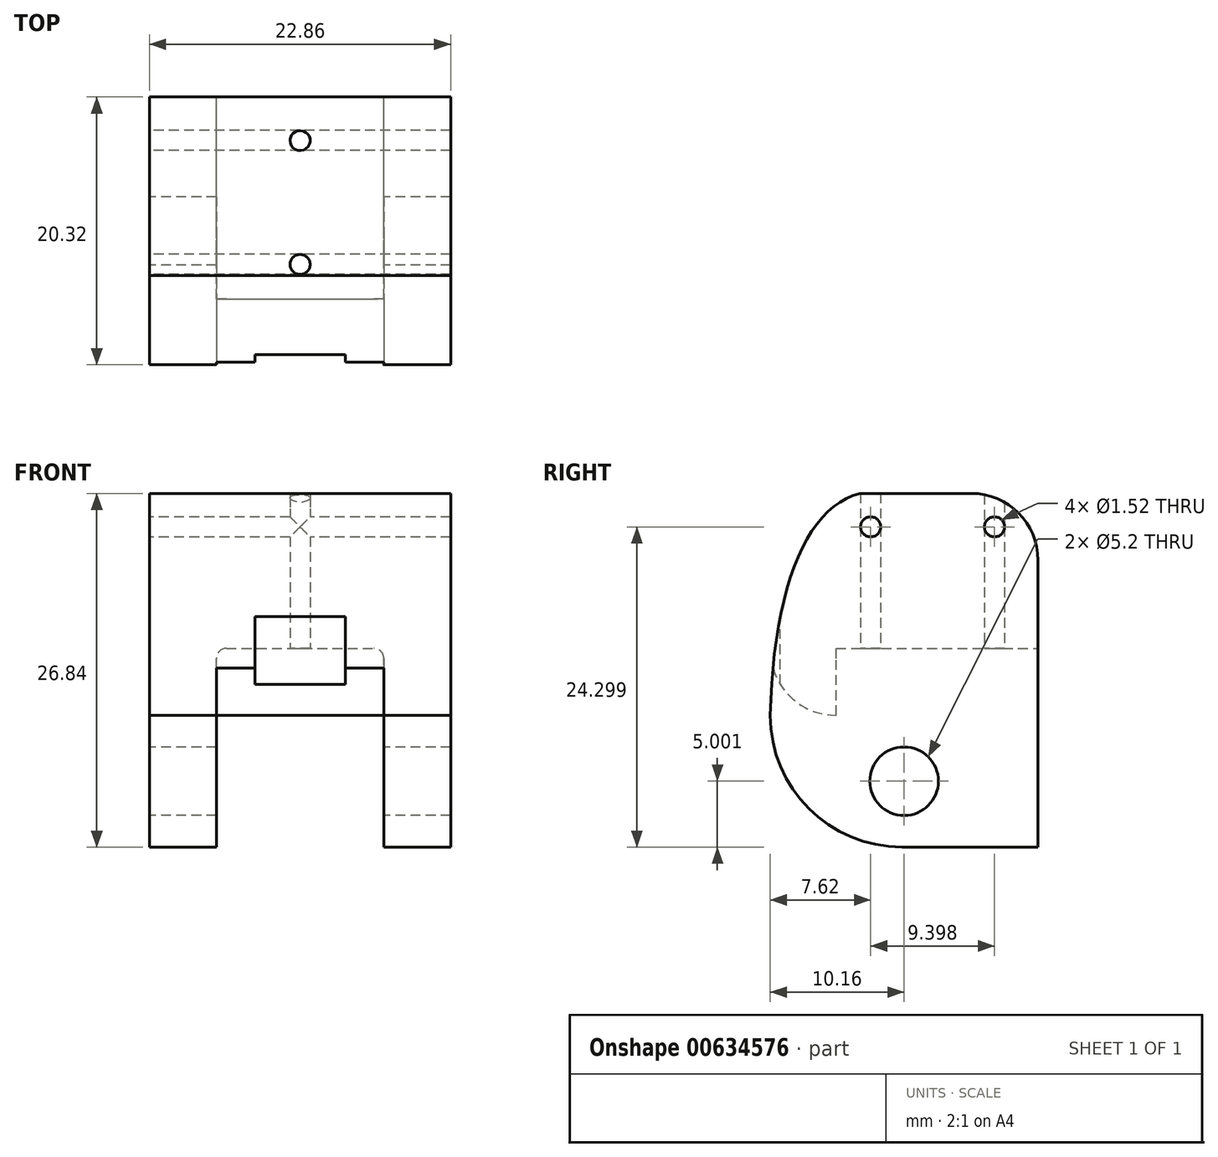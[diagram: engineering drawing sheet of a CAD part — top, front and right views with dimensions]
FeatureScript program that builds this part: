
annotation { "Feature Type Name" : "Feature", "Feature Type Description" : "" }
export const myFeature = defineFeature(function(context is Context, id is Id, definition is map)
    precondition{}
    {
        {
            var Q0;
            Q0=qCreatedBy(makeId("Front.planeOp"),FACE);
            var sketch = newSketch(context, id + "F0", { "sketchPlane" : qUnion([Q0])});
            skLineSegment(sketch, "E0.top", {"start": v(11.43, -13.42) * mm, "end": v(6.35, -13.42) * mm});
            skLineSegment(sketch, "E0.left", {"start": v(11.43, 13.42) * mm, "end": v(11.43, -13.42) * mm});
            skLineSegment(sketch, "E0.right", {"start": v(-11.43, 13.42) * mm, "end": v(-11.43, -13.42) * mm});
            skPoint(sketch, "E0.middle", {"position": v(0, 0) * mm});
            skLineSegment(sketch, "E1.left", {"start": v(6.35, -13.42) * mm, "end": v(6.35, -3.42) * mm});
            skLineSegment(sketch, "E2.trimOffspring", {"start": v(-6.35, -13.42) * mm, "end": v(-11.43, -13.42) * mm});
            skLineSegment(sketch, "E3", {"start": v(-11.43, 13.42) * mm, "end": v(11.43, 13.42) * mm});
            skLineSegment(sketch, "E4", {"start": v(-6.35, -13.42) * mm, "end": v(-6.35, -3.42) * mm});
            skLineSegment(sketch, "E5", {"start": v(-6.35, -3.42) * mm, "end": v(6.35, -3.42) * mm});
            skSolve(sketch);
        }
        {
            var Q0;
            Q0=makeQuery(id+"F0.imprint","IMPRINT",FACE,{"disambiguationData":[TD([[makeQuery(id+"F0.imprint","IMPRINT",EDGE,{"derivedFrom":sQuery(id+"F0.wireOp",EDGE,"E0.bottom")}),1.0]])]});
            var Q1;
            Q1=makeQuery(id+"F0.imprint","IMPRINT",FACE,{"disambiguationData":[TD([[makeQuery(id+"F0.imprint","IMPRINT",EDGE,{"derivedFrom":sQuery(id+"F0.wireOp",EDGE,"E0.top")}),-1.0]])]});
            extrude(context, id + "F1", {"entities" : qUnion([Q0, Q1]), "endBound" : BoundingType.SYMMETRIC, "depth" : 20.32 * mm, "offsetDistance" : 25.4 * mm});
        }
        {
            var Q0;
            Q0=makeQuery(id+"F1.opExtrude","SWEPT_FACE",FACE,{"disambiguationData":[OSD([sQuery(id+"F0.wireOp",EDGE,"E0.right")])]});
            var sketch = newSketch(context, id + "F2", { "sketchPlane" : qUnion([Q0])});
            skPoint(sketch, "E6.endSnap0", {"position": v(0, -13.42) * mm});
            skCircle(sketch, "E7", {"center": v(0, -8.42) * mm, "radius": 2.6 * mm});
            skSolve(sketch);
        }
        {
            var Q0;
            Q0=makeQuery(id+"F2.imprint","IMPRINT",FACE,{"disambiguationData":[TD([[makeQuery(id+"F2.imprint","IMPRINT",EDGE,{"derivedFrom":sQuery(id+"F2.wireOp",EDGE,"E7")}),1.0]])]});
            extrude(context, id + "F3", {"entities" : qUnion([Q0]), "operationType" : NewBodyOperationType.REMOVE, "endBound" : BoundingType.THROUGH_ALL, "oppositeDirection" : true, "depth" : 25.4 * mm, "offsetDistance" : 25.4 * mm});
        }
        {
            var Q0;
            Q0=makeQuery(id+"F1.opExtrude","CAP_EDGE",EDGE,{"disambiguationData":[OSD([sQuery(id+"F0.wireOp",EDGE,"E0.top")])],"isStart":false});
            var Q1;
            Q1=makeQuery(id+"F1.opExtrude","CAP_EDGE",EDGE,{"disambiguationData":[OSD([sQuery(id+"F0.wireOp",EDGE,"E2.trimOffspring")])],"isStart":false});
            fillet(context, id + "F4", {"entities" : qUnion([Q0, Q1]), "radius" : 10 * mm, "tangentPropagation" : true, "allowEdgeOverflow" : false});
        }
        {
            var Q0;
            Q0=makeQuery(id+"F1.opExtrude","CAP_EDGE",EDGE,{"disambiguationData":[OSD([sQuery(id+"F0.wireOp",EDGE,"n1KhcOkA-morR-dHWE-QHtQ-fdfn4GYgakT7"),sQuery(id+"F0.wireOp",EDGE,"so1H2Mnw-W18e-9x4z-PSc0-3TYgFntjAnIa")])],"isStart":false});
            var Q1;
            Q1=makeQuery(id+"F1.opExtrude","CAP_EDGE",EDGE,{"disambiguationData":[OSD([sQuery(id+"F0.wireOp",EDGE,"E5")])],"isStart":false});
            fillet(context, id + "F5", {"entities" : qUnion([Q0, Q1]), "radius" : 5 * mm, "tangentPropagation" : true, "allowEdgeOverflow" : false});
        }
        {
            var Q0;
            Q0=makeQuery(id+"F1.opExtrude","SWEPT_FACE",FACE,{"disambiguationData":[OSD([sQuery(id+"F0.wireOp",EDGE,"E0.right")])]});
            var sketch = newSketch(context, id + "F6", { "sketchPlane" : qUnion([Q0])});
            skLineSegment(sketch, "E8", {"start": v(10.16, 13.42) * mm, "end": v(10.16, -3.42) * mm});
            skEllipse(sketch, "E9", {"center": v(-7.08, -25.89) * mm, "majorRadius": 40.68 * mm, "minorRadius": 14.2 * mm, "majorAxis": v(0.26, 0.97)});
            skPoint(sketch, "E10", {"position": v(0, 13.42) * mm});
            skLineSegment(sketch, "E11", {"start": v(10.16, 13.42) * mm, "end": v(3.39, 13.42) * mm});
            skSolve(sketch);
        }
        {
            var Q0;
            {var subQ0=sQuery(id+"F6.wireOp",EDGE,"E8");Q0=makeQuery(id+"F6.imprint","IMPRINT",FACE,{"disambiguationData":[TD([[makeQuery(id+"F6.imprint","IMPRINT",EDGE,{"derivedFrom":subQ0}),-1.0]])]});}
            extrude(context, id + "F7", {"entities" : qUnion([Q0]), "operationType" : NewBodyOperationType.REMOVE, "endBound" : BoundingType.THROUGH_ALL, "oppositeDirection" : true, "depth" : 25.4 * mm, "offsetDistance" : 25.4 * mm});
        }
        {
            var Q0;
            Q0=makeQuery(id+"F1.opExtrude","CAP_EDGE",EDGE,{"disambiguationData":[OSD([sQuery(id+"F0.wireOp",EDGE,"E3")])],"isStart":true});
            fillet(context, id + "F8", {"entities" : qUnion([Q0]), "radius" : 5.08 * mm, "tangentPropagation" : true, "allowEdgeOverflow" : false});
        }
        {
            var Q0;
            Q0=makeQuery(id+"F1.opExtrude","SWEPT_FACE",FACE,{"disambiguationData":[OSD([sQuery(id+"F0.wireOp",EDGE,"E5")])]});
            var sketch = newSketch(context, id + "F9", { "sketchPlane" : qUnion([Q0])});
            skLineSegment(sketch, "E12", {"start": v(0, -10.16) * mm, "end": v(0, -7.62) * mm});
            skCircle(sketch, "E13", {"center": v(0, -6.86) * mm, "radius": 0.76 * mm});
            skCircle(sketch, "E14", {"center": v(0, 2.54) * mm, "radius": 0.76 * mm});
            skLineSegment(sketch, "E15", {"start": v(0, 10.16) * mm, "end": v(0, 3.3) * mm});
            skLineSegment(sketch, "E16", {"start": v(-11.43, 10.16) * mm, "end": v(11.43, 10.16) * mm});
            skSolve(sketch);
        }
        {
            var Q0;
            Q0=makeQuery(id+"F9.imprint","IMPRINT",FACE,{"disambiguationData":[TD([[makeQuery(id+"F9.imprint","IMPRINT",EDGE,{"derivedFrom":sQuery(id+"F9.wireOp",EDGE,"E14")}),1.0]])]});
            var Q1;
            Q1=makeQuery(id+"F9.imprint","IMPRINT",FACE,{"disambiguationData":[TD([[makeQuery(id+"F9.imprint","IMPRINT",EDGE,{"derivedFrom":sQuery(id+"F9.wireOp",EDGE,"E13")}),1.0]])]});
            extrude(context, id + "F10", {"entities" : qUnion([Q0, Q1]), "operationType" : NewBodyOperationType.REMOVE, "endBound" : BoundingType.THROUGH_ALL, "oppositeDirection" : true, "depth" : 25.4 * mm, "offsetDistance" : 25.4 * mm});
        }
        {
            var Q0;
            Q0=makeQuery(id+"F1.opExtrude","SWEPT_FACE",FACE,{"disambiguationData":[OSD([sQuery(id+"F0.wireOp",EDGE,"E0.right")])]});
            var sketch = newSketch(context, id + "F11", { "sketchPlane" : qUnion([Q0])});
            skLineSegment(sketch, "E17", {"start": v(-7.62, 13.42) * mm, "end": v(-7.62, 10.88) * mm});
            skLineSegment(sketch, "E18", {"start": v(-7.62, 10.88) * mm, "end": v(-10.16, 10.88) * mm});
            skLineSegment(sketch, "E19", {"start": v(10.16, 10.88) * mm, "end": v(3.3, 10.88) * mm});
            skLineSegment(sketch, "E20", {"start": v(3.3, 10.88) * mm, "end": v(3.3, 13.42) * mm});
            skCircle(sketch, "E21", {"center": v(-6.86, 10.88) * mm, "radius": 0.76 * mm});
            skCircle(sketch, "E22", {"center": v(2.54, 10.88) * mm, "radius": 0.76 * mm});
            skLineSegment(sketch, "E23", {"start": v(-10.16, -13.42) * mm, "end": v(10.16, -13.42) * mm});
            skLineSegment(sketch, "E24", {"start": v(10.16, -13.42) * mm, "end": v(10.16, 10.88) * mm});
            skSolve(sketch);
        }
        {
            var Q0;
            Q0=makeQuery(id+"F11.imprint","IMPRINT",FACE,{"disambiguationData":[TD([[makeQuery(id+"F11.imprint","IMPRINT",EDGE,{"derivedFrom":sQuery(id+"F11.wireOp",EDGE,"E21")}),1.0]])]});
            var Q1;
            Q1=makeQuery(id+"F11.imprint","IMPRINT",FACE,{"disambiguationData":[TD([[makeQuery(id+"F11.imprint","IMPRINT",EDGE,{"derivedFrom":sQuery(id+"F11.wireOp",EDGE,"E22")}),1.0]])]});
            extrude(context, id + "F12", {"entities" : qUnion([Q0, Q1]), "operationType" : NewBodyOperationType.REMOVE, "endBound" : BoundingType.THROUGH_ALL, "oppositeDirection" : true, "depth" : 25.4 * mm, "offsetDistance" : 25.4 * mm});
        }
        {
            var Q0;
            {var subQ0=sQuery(id+"F0.wireOp",EDGE,"E2.trimOffspring");var subQ1=sQuery(id+"F0.wireOp",EDGE,"E0.right");var subQ2=sQuery(id+"F0.wireOp",EDGE,"E0.top");Q0=makeQuery(id+"F7.boolean.opBoolean","MERGE",EDGE,{"derivedFrom":[makeQuery(id+"F4.opFillet","BLEND_EDGE",EDGE,{"blendedFrom":[makeQuery(id+"F1.opExtrude","CAP_EDGE",EDGE,{"disambiguationData":[OSD([subQ2])],"isStart":false}),makeQuery(id+"F1.opExtrude","CAP_FACE",FACE,{"disambiguationData":[OSD([subQ2,sQuery(id+"F0.wireOp",EDGE,"E0.left"),subQ1,sQuery(id+"F0.wireOp",EDGE,"E1.left"),subQ0,sQuery(id+"F0.wireOp",EDGE,"E3"),sQuery(id+"F0.wireOp",EDGE,"E4"),sQuery(id+"F0.wireOp",EDGE,"E5")])],"isStart":false})],"blendedInto":[makeQuery(id+"F1.opExtrude","CAP_FACE",FACE,{"disambiguationData":[OSD([subQ2,sQuery(id+"F0.wireOp",EDGE,"E0.left"),subQ1,sQuery(id+"F0.wireOp",EDGE,"E1.left"),subQ0,sQuery(id+"F0.wireOp",EDGE,"E3"),sQuery(id+"F0.wireOp",EDGE,"E4"),sQuery(id+"F0.wireOp",EDGE,"E5")])],"isStart":false})]}),makeQuery(id+"F7.opExtrude","SWEPT_EDGE",EDGE,{"disambiguationData":[OSD([subQ1,subQ0,sQuery(id+"F6.wireOp",EDGE,"E8"),sQuery(id+"F6.wireOp",EDGE,"E9")])]})]});}
            cPlane(context, id + "F13", {"entities" : qUnion([Q0]), "cplaneType" : CPlaneType.LINE_ANGLE, "offset" : 25.4 * mm, "angle" : 0 * degree, "width" : 152.4 * mm, "height" : 152.4 * mm});
        }
        {
            var Q0;
            Q0=qCreatedBy(id+"F13.planeOp",FACE);
            var sketch = newSketch(context, id + "F14", { "sketchPlane" : qUnion([Q0])});
            skLineSegment(sketch, "E25", {"start": v(-11.43, 13.42) * mm, "end": v(11.43, 13.42) * mm});
            skLineSegment(sketch, "E26", {"start": v(0, 13.42) * mm, "end": v(0, 10.37) * mm});
            skCircle(sketch, "E27", {"center": v(0, 6.94) * mm, "radius": 3.43 * mm});
            skLineSegment(sketch, "E28", {"start": v(-3.43, 6.94) * mm, "end": v(0, 6.94) * mm});
            skLineSegment(sketch, "E29", {"start": v(3.43, 6.94) * mm, "end": v(0, 6.94) * mm});
            skLineSegment(sketch, "E30", {"start": v(-3.43, 6.94) * mm, "end": v(-3.43, -3.42) * mm});
            skLineSegment(sketch, "E31", {"start": v(-3.43, -3.42) * mm, "end": v(3.43, -3.42) * mm});
            skLineSegment(sketch, "E32", {"start": v(3.43, -3.42) * mm, "end": v(3.43, 6.94) * mm});
            skSolve(sketch);
        }
        {
            var Q0;
            Q0=makeQuery(id+"F1.opExtrude","CAP_FACE",FACE,{"disambiguationData":[OSD([sQuery(id+"F0.wireOp",EDGE,"E0.top"),sQuery(id+"F0.wireOp",EDGE,"E0.left"),sQuery(id+"F0.wireOp",EDGE,"E0.right"),sQuery(id+"F0.wireOp",EDGE,"E1.left"),sQuery(id+"F0.wireOp",EDGE,"E2.trimOffspring"),sQuery(id+"F0.wireOp",EDGE,"E3"),sQuery(id+"F0.wireOp",EDGE,"E4"),sQuery(id+"F0.wireOp",EDGE,"E5")])],"isStart":true});
            var sketch = newSketch(context, id + "F15", { "sketchPlane" : qUnion([Q0])});
            skLineSegment(sketch, "E33.top", {"start": v(0, 1.66) * mm, "end": v(5.59, 1.66) * mm});
            skLineSegment(sketch, "E33.right", {"start": v(6.35, -3.42) * mm, "end": v(6.35, 0.9) * mm});
            skLineSegment(sketch, "E34.bottom", {"start": v(0, 1.66) * mm, "end": v(0, 1.66) * mm});
            skLineSegment(sketch, "E35.bottom", {"start": v(0, 1.66) * mm, "end": v(-5.59, 1.66) * mm});
            skLineSegment(sketch, "E35.right", {"start": v(-6.35, 0.9) * mm, "end": v(-6.35, -3.42) * mm});
            skArc(sketch, "E36.filletArc", {"start": v(6.35, 0.9) * mm, "mid": v(6.13, 1.44) * mm, "end": v(5.59, 1.66) * mm});
            skArc(sketch, "E37.filletArc", {"start": v(-5.59, 1.66) * mm, "mid": v(-6.13, 1.44) * mm, "end": v(-6.35, 0.9) * mm});
            skLineSegment(sketch, "E38", {"start": v(0, 1.66) * mm, "end": v(0, -3.42) * mm});
            skLineSegment(sketch, "E39", {"start": v(6.35, -3.42) * mm, "end": v(6.35, -3.42) * mm});
            skLineSegment(sketch, "E40.trimOffspring", {"start": v(-6.35, -3.42) * mm, "end": v(-6.35, -3.42) * mm});
            skLineSegment(sketch, "E41", {"start": v(-6.35, -3.42) * mm, "end": v(6.35, -3.42) * mm});
            skSolve(sketch);
        }
        {
            var Q0;
            {var subQ5=sQuery(id+"F15.wireOp",EDGE,"E35.bottom");Q0=makeQuery(id+"F15.imprint","IMPRINT",FACE,{"disambiguationData":[TD([[makeQuery(id+"F15.imprint","IMPRINT",EDGE,{"derivedFrom":subQ5}),1.0]])]});}
            var Q1;
            {var subQ5=sQuery(id+"F15.wireOp",EDGE,"E33.top");Q1=makeQuery(id+"F15.imprint","IMPRINT",FACE,{"disambiguationData":[TD([[makeQuery(id+"F15.imprint","IMPRINT",EDGE,{"derivedFrom":subQ5}),-1.0]])]});}
            var Q2;
            {var subQ0=sQuery(id+"F0.wireOp",EDGE,"E5");Q2=makeQuery(id+"F5.opFillet","BLEND_VERTEX",VERTEX,{"blendedFrom":[makeQuery(id+"F1.opExtrude","CAP_EDGE",EDGE,{"disambiguationData":[OSD([subQ0])],"isStart":false}),makeQuery(id+"F1.opExtrude","SWEPT_FACE",FACE,{"disambiguationData":[OSD([subQ0])]}),makeQuery(id+"F1.opExtrude","SWEPT_FACE",FACE,{"disambiguationData":[OSD([sQuery(id+"F0.wireOp",EDGE,"E4")])]})],"blendedInto":[makeQuery(id+"F1.opExtrude","SWEPT_FACE",FACE,{"disambiguationData":[OSD([subQ0])]}),makeQuery(id+"F1.opExtrude","SWEPT_FACE",FACE,{"disambiguationData":[OSD([sQuery(id+"F0.wireOp",EDGE,"E4")])]})]});}
            extrude(context, id + "F16", {"entities" : qUnion([Q0, Q1]), "operationType" : NewBodyOperationType.REMOVE, "endBound" : BoundingType.UP_TO_VERTEX, "oppositeDirection" : true, "depth" : 13.97 * mm, "endBoundEntityVertex" : qUnion([Q2]), "offsetDistance" : 25.4 * mm});
        }
        {
            var Q0;
            {var subQ3=sQuery(id+"F14.wireOp",EDGE,"E28");Q0=makeQuery(id+"F14.imprint","IMPRINT",FACE,{"disambiguationData":[TD([[makeQuery(id+"F14.imprint","IMPRINT",EDGE,{"derivedFrom":subQ3}),1.0]])]});}
            var Q1;
            {var subQ0=sQuery(id+"F14.wireOp",EDGE,"E28");Q1=makeQuery(id+"F14.imprint","IMPRINT",FACE,{"disambiguationData":[TD([[makeQuery(id+"F14.imprint","IMPRINT",EDGE,{"derivedFrom":subQ0}),-1.0]])]});}
            var Q2;
            {var subQ0=sQuery(id+"F14.wireOp",EDGE,"E30");Q2=makeQuery(id+"F14.imprint","IMPRINT",FACE,{"disambiguationData":[TD([[makeQuery(id+"F14.imprint","IMPRINT",EDGE,{"derivedFrom":subQ0}),1.0]])]});}
            extrude(context, id + "F17", {"entities" : qUnion([Q0, Q1, Q2]), "operationType" : NewBodyOperationType.REMOVE, "oppositeDirection" : true, "depth" : 0.76 * mm, "offsetDistance" : 25.4 * mm});
        }
    });
